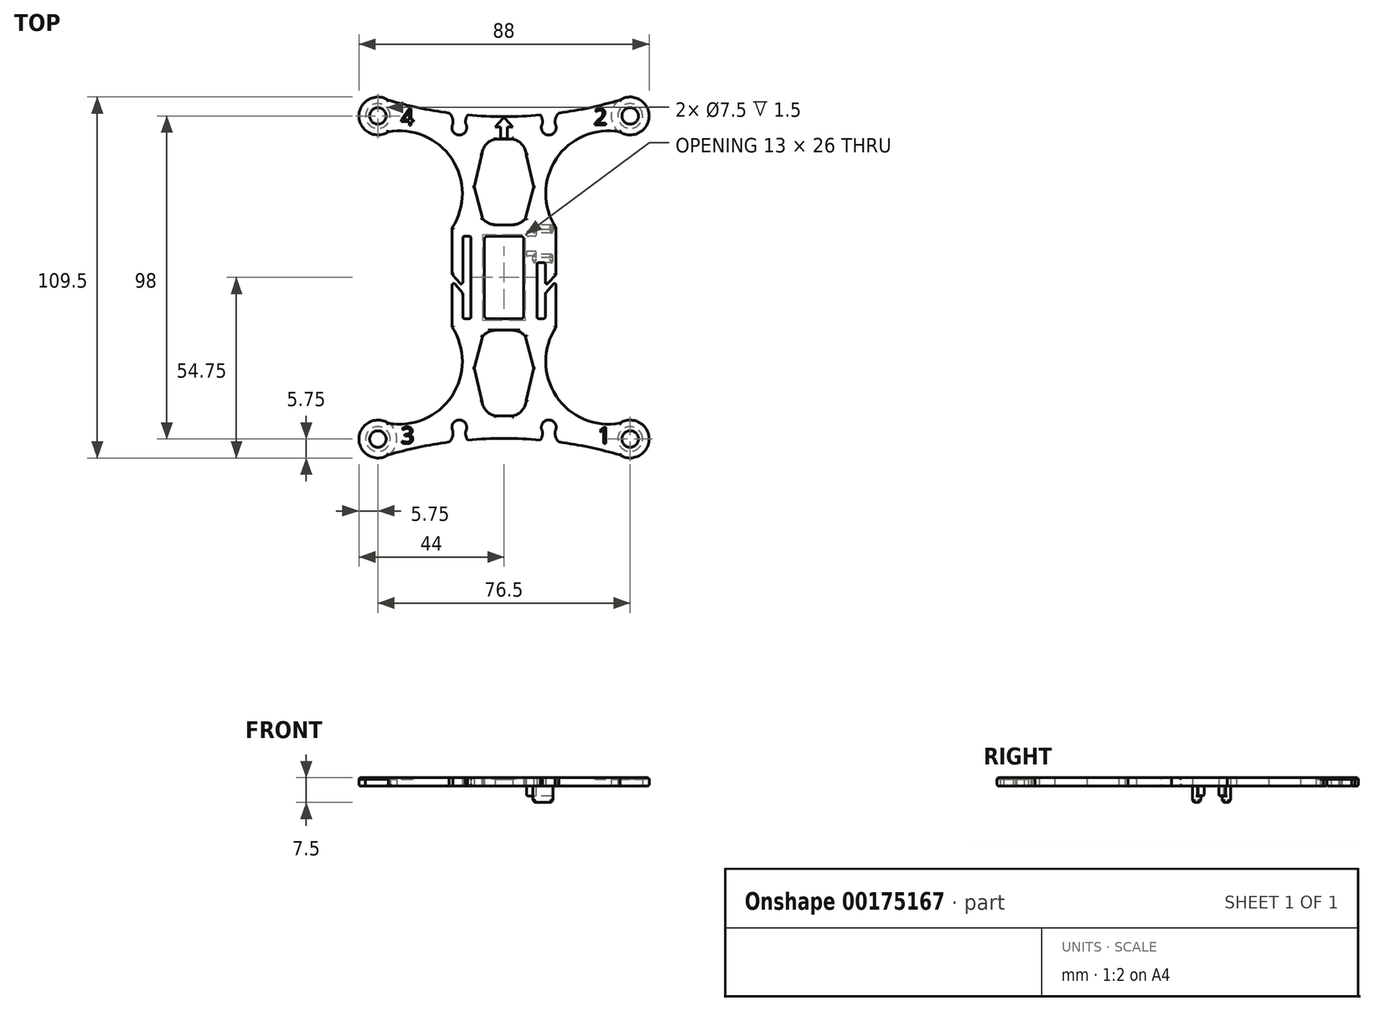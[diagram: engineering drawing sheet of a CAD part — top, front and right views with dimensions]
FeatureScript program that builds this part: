
annotation { "Feature Type Name" : "Feature", "Feature Type Description" : "" }
export const myFeature = defineFeature(function(context is Context, id is Id, definition is map)
    precondition{}
    {
        {
            var Q0;
            Q0=qCreatedBy(makeId("Top.planeOp"),FACE);
            var sketch = newSketch(context, id + "F0", { "sketchPlane" : qUnion([Q0])});
            skPoint(sketch, "E0.middle", {"position": v(0, 0) * mm});
            skCircle(sketch, "E1", {"center": v(-38.25, 49) * mm, "radius": 5.75 * mm});
            skCircle(sketch, "E2.MirrorC", {"center": v(38.25, 49) * mm, "radius": 5.75 * mm});
            skCircle(sketch, "E3.MirrorC", {"center": v(-38.25, -49) * mm, "radius": 5.75 * mm});
            skCircle(sketch, "E4.MirrorC", {"center": v(38.25, -49) * mm, "radius": 5.75 * mm});
            skArc(sketch, "E5", {"start": v(-35.12, 53.82) * mm, "mid": v(-25.97, 51.52) * mm, "end": v(-16.67, 49.9) * mm});
            skCircle(sketch, "E6", {"center": v(-38.25, 49) * mm, "radius": 3.75 * mm});
            skCircle(sketch, "E7.MirrorC", {"center": v(38.25, 49) * mm, "radius": 3.75 * mm});
            skCircle(sketch, "E8.MirrorC", {"center": v(38.25, -49) * mm, "radius": 3.75 * mm});
            skCircle(sketch, "E9.MirrorC", {"center": v(-38.25, -49) * mm, "radius": 3.75 * mm});
            skPoint(sketch, "E10.MirrorP", {"position": v(-9, -27.55) * mm});
            skArc(sketch, "E11.MirrorCS", {"start": v(-2.66, -42) * mm, "mid": v(-5.49, -40.33) * mm, "end": v(-6.7, -37.29) * mm});
            skArc(sketch, "E12.MirrorCS", {"start": v(-2.66, -16) * mm, "mid": v(-4.79, -16.51) * mm, "end": v(-6.5, -17.87) * mm});
            skLineSegment(sketch, "E13", {"start": v(-6.5, -17.87) * mm, "end": v(-9, -27.55) * mm});
            skLineSegment(sketch, "E14", {"start": v(-6.7, -37.29) * mm, "end": v(-9, -27.55) * mm});
            skArc(sketch, "E15.MirrorCS", {"start": v(2.66, -16) * mm, "mid": v(4.79, -16.51) * mm, "end": v(6.5, -17.87) * mm});
            skLineSegment(sketch, "E16.MirrorCS", {"start": v(6.5, -17.87) * mm, "end": v(9, -27.55) * mm});
            skLineSegment(sketch, "E17.MirrorCS", {"start": v(6.7, -37.29) * mm, "end": v(9, -27.55) * mm});
            skArc(sketch, "E18.MirrorCS", {"start": v(2.66, -42) * mm, "mid": v(5.49, -40.33) * mm, "end": v(6.7, -37.29) * mm});
            skLineSegment(sketch, "E19", {"start": v(-2.66, -16) * mm, "end": v(2.66, -16) * mm});
            skLineSegment(sketch, "E20", {"start": v(2.66, -42) * mm, "end": v(-2.66, -42) * mm});
            skLineSegment(sketch, "E21.MirrorCS", {"start": v(-2.66, 16) * mm, "end": v(2.66, 16) * mm});
            skArc(sketch, "E22.MirrorCS", {"start": v(-2.66, 16) * mm, "mid": v(-4.79, 16.51) * mm, "end": v(-6.5, 17.87) * mm});
            skLineSegment(sketch, "E23.MirrorCS", {"start": v(-6.5, 17.87) * mm, "end": v(-9, 27.55) * mm});
            skArc(sketch, "E24.MirrorCS", {"start": v(2.66, 16) * mm, "mid": v(4.79, 16.51) * mm, "end": v(6.5, 17.87) * mm});
            skLineSegment(sketch, "E25.MirrorCS", {"start": v(6.5, 17.87) * mm, "end": v(9, 27.55) * mm});
            skLineSegment(sketch, "E26.MirrorCS", {"start": v(-6.7, 37.29) * mm, "end": v(-9, 27.55) * mm});
            skLineSegment(sketch, "E27.MirrorCS", {"start": v(6.7, 37.29) * mm, "end": v(9, 27.55) * mm});
            skArc(sketch, "E28.MirrorCS", {"start": v(2.66, 42) * mm, "mid": v(5.49, 40.33) * mm, "end": v(6.7, 37.29) * mm});
            skLineSegment(sketch, "E29.MirrorCS", {"start": v(2.66, 42) * mm, "end": v(-2.66, 42) * mm});
            skArc(sketch, "E30.MirrorCS", {"start": v(-2.66, 42) * mm, "mid": v(-5.49, 40.33) * mm, "end": v(-6.7, 37.29) * mm});
            skArc(sketch, "E31", {"start": v(-15.79, 15) * mm, "mid": v(-15.82, 36) * mm, "end": v(-35.17, 44.14) * mm});
            skArc(sketch, "E32.MirrorCS", {"start": v(-35.12, -53.82) * mm, "mid": v(-25.97, -51.52) * mm, "end": v(-16.67, -49.9) * mm});
            skArc(sketch, "E33.MirrorCS", {"start": v(15.79, 15) * mm, "mid": v(15.82, 36) * mm, "end": v(35.17, 44.14) * mm});
            skArc(sketch, "E34.MirrorCS", {"start": v(15.79, -15) * mm, "mid": v(15.82, -36) * mm, "end": v(35.17, -44.14) * mm});
            skArc(sketch, "E35.MirrorCS", {"start": v(-15.79, -15) * mm, "mid": v(-15.82, -36) * mm, "end": v(-35.17, -44.14) * mm});
            skLineSegment(sketch, "E36", {"start": v(-15.79, 15) * mm, "end": v(15.79, 15) * mm, "construction": true});
            skLineSegment(sketch, "E37.MirrorCS", {"start": v(12, -12.5) * mm, "end": v(10.5, -12.5) * mm});
            skArc(sketch, "E38.MirrorCS", {"start": v(12.5, -12) * mm, "mid": v(12.35, -12.35) * mm, "end": v(12, -12.5) * mm});
            skArc(sketch, "E39.MirrorCS", {"start": v(10.5, -12.5) * mm, "mid": v(10.15, -12.35) * mm, "end": v(10, -12) * mm});
            skArc(sketch, "E40.trimOffspring", {"start": v(-11.03, 49.28) * mm, "mid": v(0, 48.79) * mm, "end": v(11.03, 49.28) * mm});
            skArc(sketch, "E41.MirrorCS", {"start": v(-11.6, 46.53) * mm, "mid": v(-11.6, 47.96) * mm, "end": v(-11.03, 49.28) * mm});
            skLineSegment(sketch, "E42.bottom", {"start": v(-5, 12.5) * mm, "end": v(5, 12.5) * mm});
            skLineSegment(sketch, "E42.top", {"start": v(-5, -12.5) * mm, "end": v(5, -12.5) * mm});
            skLineSegment(sketch, "E42.left", {"start": v(-6, 11.5) * mm, "end": v(-6, -11.5) * mm});
            skLineSegment(sketch, "E42.right", {"start": v(6, 11.5) * mm, "end": v(6, -11.5) * mm});
            skPoint(sketch, "E43.visualSharp", {"position": v(-6, 12.5) * mm});
            skArc(sketch, "E43.filletArc", {"start": v(-5, 12.5) * mm, "mid": v(-5.7, 12.2) * mm, "end": v(-6, 11.5) * mm});
            skArc(sketch, "E44.filletArc", {"start": v(6, 11.5) * mm, "mid": v(5.7, 12.2) * mm, "end": v(5, 12.5) * mm});
            skPoint(sketch, "E45.visualSharp", {"position": v(6, -12.5) * mm});
            skArc(sketch, "E45.filletArc", {"start": v(5, -12.5) * mm, "mid": v(5.7, -12.2) * mm, "end": v(6, -11.5) * mm});
            skPoint(sketch, "E46.visualSharp", {"position": v(-6, -12.5) * mm});
            skArc(sketch, "E46.filletArc", {"start": v(-6, -11.5) * mm, "mid": v(-5.7, -12.2) * mm, "end": v(-5, -12.5) * mm});
            skLineSegment(sketch, "E47", {"start": v(-15.79, -15) * mm, "end": v(-15.79, -2.33) * mm});
            skLineSegment(sketch, "E48", {"start": v(-15.79, 15) * mm, "end": v(-15.79, 1) * mm});
            skLineSegment(sketch, "E49.MirrorCS", {"start": v(-10, -12) * mm, "end": v(-10, 12) * mm});
            skLineSegment(sketch, "E50.MirrorCS", {"start": v(-12.5, -12) * mm, "end": v(-12.5, -4.77) * mm});
            skLineSegment(sketch, "E51.MirrorCS", {"start": v(-12, 12.5) * mm, "end": v(-10.5, 12.5) * mm});
            skArc(sketch, "E52.MirrorCS", {"start": v(-10, 12) * mm, "mid": v(-10.15, 12.35) * mm, "end": v(-10.5, 12.5) * mm});
            skArc(sketch, "E53.MirrorCS", {"start": v(-12, 12.5) * mm, "mid": v(-12.35, 12.35) * mm, "end": v(-12.5, 12) * mm});
            skArc(sketch, "E54.MirrorCS", {"start": v(-10.5, -12.5) * mm, "mid": v(-10.15, -12.35) * mm, "end": v(-10, -12) * mm});
            skLineSegment(sketch, "E55.MirrorCS", {"start": v(-12, -12.5) * mm, "end": v(-10.5, -12.5) * mm});
            skArc(sketch, "E56.MirrorCS", {"start": v(-12.5, -12) * mm, "mid": v(-12.35, -12.35) * mm, "end": v(-12, -12.5) * mm});
            skLineSegment(sketch, "E57", {"start": v(-14.91, -2) * mm, "end": v(-12.5, -4.77) * mm});
            skLineSegment(sketch, "E58", {"start": v(-15.79, 1) * mm, "end": v(-13.38, -1.76) * mm});
            skLineSegment(sketch, "E59.trimOffspring", {"start": v(-12.5, -1.43) * mm, "end": v(-12.5, 12) * mm});
            skPoint(sketch, "E60.visualSharp", {"position": v(-15.79, -1) * mm});
            skArc(sketch, "E60.filletArc", {"start": v(-14.91, -2) * mm, "mid": v(-15.47, -1.86) * mm, "end": v(-15.79, -2.33) * mm});
            skArc(sketch, "E61.filletArc", {"start": v(-13.38, -1.76) * mm, "mid": v(-12.82, -1.9) * mm, "end": v(-12.5, -1.43) * mm});
            skLineSegment(sketch, "E62.MirrorCS", {"start": v(12.5, -12) * mm, "end": v(12.5, -4.77) * mm});
            skLineSegment(sketch, "E63.MirrorCS", {"start": v(10, -12) * mm, "end": v(10, 4) * mm});
            skLineSegment(sketch, "E64.MirrorCS", {"start": v(14.91, -2) * mm, "end": v(12.5, -4.77) * mm});
            skLineSegment(sketch, "E65.MirrorCS", {"start": v(15.79, -15) * mm, "end": v(15.79, -2.33) * mm});
            skArc(sketch, "E66.MirrorCS", {"start": v(14.91, -2) * mm, "mid": v(15.47, -1.86) * mm, "end": v(15.79, -2.33) * mm});
            skArc(sketch, "E67.MirrorCS", {"start": v(13.38, -1.76) * mm, "mid": v(12.82, -1.9) * mm, "end": v(12.5, -1.43) * mm});
            skLineSegment(sketch, "E68.MirrorCS", {"start": v(12.5, -1.43) * mm, "end": v(12.5, 4) * mm});
            skLineSegment(sketch, "E69.MirrorCS", {"start": v(15.79, 1) * mm, "end": v(13.38, -1.76) * mm});
            skLineSegment(sketch, "E70.MirrorCS", {"start": v(15.79, 15) * mm, "end": v(15.79, 1) * mm});
            skPoint(sketch, "E71", {"position": v(10, 4.5) * mm});
            skPoint(sketch, "E72", {"position": v(12.5, 4.5) * mm});
            skLineSegment(sketch, "E73", {"start": v(10.5, 4.5) * mm, "end": v(12, 4.5) * mm});
            skArc(sketch, "E74.filletArc", {"start": v(10.5, 4.5) * mm, "mid": v(10.15, 4.35) * mm, "end": v(10, 4) * mm});
            skArc(sketch, "E75.filletArc", {"start": v(12.5, 4) * mm, "mid": v(12.35, 4.35) * mm, "end": v(12, 4.5) * mm});
            skPoint(sketch, "E76.visualSharp", {"position": v(8.79, 4.5) * mm});
            skPoint(sketch, "E77.visualSharp", {"position": v(14.79, 4.5) * mm});
            skArc(sketch, "E78.trimOffspring", {"start": v(16.67, 49.9) * mm, "mid": v(25.97, 51.52) * mm, "end": v(35.12, 53.82) * mm});
            skArc(sketch, "E79.trimOffspring", {"start": v(16.67, -49.9) * mm, "mid": v(25.97, -51.52) * mm, "end": v(35.12, -53.82) * mm});
            skArc(sketch, "E80.trimOffspring", {"start": v(-11.03, -49.28) * mm, "mid": v(0, -48.79) * mm, "end": v(11.03, -49.28) * mm});
            skLineSegment(sketch, "E81", {"start": v(17.22, 49.98) * mm, "end": v(17.22, 49.98) * mm});
            skLineSegment(sketch, "E82.MirrorCS", {"start": v(17.22, -49.98) * mm, "end": v(17.22, -49.98) * mm});
            skArc(sketch, "E83.MirrorCS", {"start": v(-15.54, 46.53) * mm, "mid": v(-15.65, 48.37) * mm, "end": v(-16.67, 49.9) * mm});
            skArc(sketch, "E84.trimOffspring", {"start": v(-15.54, 46.53) * mm, "mid": v(-13.57, 43.2) * mm, "end": v(-11.6, 46.53) * mm});
            skArc(sketch, "E85.MirrorCS", {"start": v(11.6, 46.53) * mm, "mid": v(11.6, 47.96) * mm, "end": v(11.03, 49.28) * mm});
            skArc(sketch, "E86.MirrorCS", {"start": v(15.54, 46.53) * mm, "mid": v(13.57, 43.2) * mm, "end": v(11.6, 46.53) * mm});
            skArc(sketch, "E87.MirrorCS", {"start": v(15.54, 46.53) * mm, "mid": v(15.65, 48.37) * mm, "end": v(16.67, 49.9) * mm});
            skArc(sketch, "E88.MirrorCS", {"start": v(15.54, -46.53) * mm, "mid": v(13.57, -43.2) * mm, "end": v(11.6, -46.53) * mm});
            skArc(sketch, "E89.MirrorCS", {"start": v(15.54, -46.53) * mm, "mid": v(15.65, -48.37) * mm, "end": v(16.67, -49.9) * mm});
            skArc(sketch, "E90.MirrorCS", {"start": v(11.6, -46.53) * mm, "mid": v(11.6, -47.96) * mm, "end": v(11.03, -49.28) * mm});
            skArc(sketch, "E91.MirrorCS", {"start": v(-15.54, -46.53) * mm, "mid": v(-15.65, -48.37) * mm, "end": v(-16.67, -49.9) * mm});
            skArc(sketch, "E92.MirrorCS", {"start": v(-11.6, -46.53) * mm, "mid": v(-11.6, -47.96) * mm, "end": v(-11.03, -49.28) * mm});
            skArc(sketch, "E93.MirrorCS", {"start": v(-15.54, -46.53) * mm, "mid": v(-13.57, -43.2) * mm, "end": v(-11.6, -46.53) * mm});
            skSolve(sketch);
        }
        {
            var Q0;
            {var subQ4=sQuery(id+"F0.wireOp",EDGE,"E5");Q0=makeQuery(id+"F0.imprint","IMPRINT",FACE,{"disambiguationData":[TD([[makeQuery(id+"F0.imprint","IMPRINT",EDGE,{"derivedFrom":subQ4}),-1.0]])]});}
            var Q1;
            {var subQ0=sQuery(id+"F0.wireOp",EDGE,"7a08c846-7200-404a-ab22-a396ae0e95b40.MirrorCS");Q1=makeQuery(id+"F0.imprint","IMPRINT",FACE,{"disambiguationData":[TD([[makeQuery(id+"F0.imprint","IMPRINT",EDGE,{"derivedFrom":subQ0}),-1.0]])]});}
            var Q2;
            {var subQ0=sQuery(id+"F0.wireOp",EDGE,"SV39OC4L-nHPT-JrW3-9Lr1-tMvvluVvlcrm");Q2=makeQuery(id+"F0.imprint","IMPRINT",FACE,{"disambiguationData":[TD([[makeQuery(id+"F0.imprint","IMPRINT",EDGE,{"derivedFrom":subQ0}),1.0]])]});}
            var Q3;
            {var subQ2=sQuery(id+"F0.wireOp",EDGE,"KmvPTI4Y-Ru9T-GGZq-2kg1-KeB8K268cKMw.top");Q3=makeQuery(id+"F0.imprint","IMPRINT",FACE,{"disambiguationData":[TD([[makeQuery(id+"F0.imprint","IMPRINT",EDGE,{"derivedFrom":subQ2}),-1.0]])]});}
            var Q4;
            Q4=makeQuery(id+"F0.imprint","IMPRINT",FACE,{"disambiguationData":[TD([[makeQuery(id+"F0.imprint","IMPRINT",EDGE,{"derivedFrom":sQuery(id+"F0.wireOp",EDGE,"TM0b15PC-G09Y-eCJG-wMI8-OMJ6jJeQZKML.top")}),1.0]])]});
            var Q5;
            Q5=makeQuery(id+"F0.imprint","IMPRINT",FACE,{"disambiguationData":[TD([[makeQuery(id+"F0.imprint","IMPRINT",EDGE,{"derivedFrom":sQuery(id+"F0.wireOp",EDGE,"3d6d2522-cb81-429b-89e0-43078ca379200.MirrorCS")}),-1.0]])]});
            var Q6;
            {var subQ1=sQuery(id+"F0.wireOp",EDGE,"f26be708-061c-449e-934f-b77e1b1d895a0.MirrorCS");Q6=makeQuery(id+"F0.imprint","IMPRINT",FACE,{"disambiguationData":[TD([[makeQuery(id+"F0.imprint","IMPRINT",EDGE,{"derivedFrom":subQ1}),-1.0]])]});}
            extrude(context, id + "F1", {"entities" : qUnion([Q0, Q1, Q2, Q3, Q4, Q5, Q6]), "depth" : 2.5 * mm});
        }
        {
            var Q0;
            Q0=makeQuery(id+"F0.imprint","IMPRINT",FACE,{"disambiguationData":[TD([[makeQuery(id+"F0.imprint","IMPRINT",EDGE,{"derivedFrom":sQuery(id+"F0.wireOp",EDGE,"E6")}),-1.0]])]});
            var Q1;
            Q1=makeQuery(id+"F0.imprint","IMPRINT",FACE,{"disambiguationData":[TD([[makeQuery(id+"F0.imprint","IMPRINT",EDGE,{"derivedFrom":sQuery(id+"F0.wireOp",EDGE,"E7.MirrorC")}),1.0]])]});
            var Q2;
            Q2=makeQuery(id+"F0.imprint","IMPRINT",FACE,{"disambiguationData":[TD([[makeQuery(id+"F0.imprint","IMPRINT",EDGE,{"derivedFrom":sQuery(id+"F0.wireOp",EDGE,"E8.MirrorC")}),-1.0]])]});
            var Q3;
            Q3=makeQuery(id+"F0.imprint","IMPRINT",FACE,{"disambiguationData":[TD([[makeQuery(id+"F0.imprint","IMPRINT",EDGE,{"derivedFrom":sQuery(id+"F0.wireOp",EDGE,"E9.MirrorC")}),1.0]])]});
            extrude(context, id + "F2", {"entities" : qUnion([Q0, Q1, Q2, Q3]), "operationType" : NewBodyOperationType.ADD, "depth" : 2 * mm});
        }
        {
            var Q0;
            Q0=makeQuery(id+"F1.opExtrude","CAP_FACE",FACE,{"disambiguationData":[OSD([sQuery(id+"F0.wireOp",EDGE,"E1"),sQuery(id+"F0.wireOp",EDGE,"E2.MirrorC"),sQuery(id+"F0.wireOp",EDGE,"E3.MirrorC"),sQuery(id+"F0.wireOp",EDGE,"E4.MirrorC"),sQuery(id+"F0.wireOp",EDGE,"E5"),sQuery(id+"F0.wireOp",EDGE,"E6"),sQuery(id+"F0.wireOp",EDGE,"E7.MirrorC"),sQuery(id+"F0.wireOp",EDGE,"E8.MirrorC"),sQuery(id+"F0.wireOp",EDGE,"E9.MirrorC"),sQuery(id+"F0.wireOp",EDGE,"vB4YpJxw-nM1r-KAMU-Z2z7-AA1Xbjjr12VQ"),sQuery(id+"F0.wireOp",EDGE,"e54bd452-817c-44b1-b4a1-4a82a5b737490.MirrorC"),sQuery(id+"F0.wireOp",EDGE,"5ae8c34d-aa19-45d0-b816-4b0481c35e6e0.MirrorC"),sQuery(id+"F0.wireOp",EDGE,"3a3e3443-e76c-4b3f-931a-bba0a9ca54bb0.MirrorC"),sQuery(id+"F0.wireOp",EDGE,"E11.MirrorCS"),sQuery(id+"F0.wireOp",EDGE,"E12.MirrorCS"),sQuery(id+"F0.wireOp",EDGE,"E13"),sQuery(id+"F0.wireOp",EDGE,"E14"),sQuery(id+"F0.wireOp",EDGE,"E15.MirrorCS"),sQuery(id+"F0.wireOp",EDGE,"E16.MirrorCS"),sQuery(id+"F0.wireOp",EDGE,"E17.MirrorCS"),sQuery(id+"F0.wireOp",EDGE,"E18.MirrorCS"),sQuery(id+"F0.wireOp",EDGE,"E19"),sQuery(id+"F0.wireOp",EDGE,"E20"),sQuery(id+"F0.wireOp",EDGE,"E21.MirrorCS"),sQuery(id+"F0.wireOp",EDGE,"E22.MirrorCS"),sQuery(id+"F0.wireOp",EDGE,"E23.MirrorCS"),sQuery(id+"F0.wireOp",EDGE,"E24.MirrorCS"),sQuery(id+"F0.wireOp",EDGE,"E25.MirrorCS"),sQuery(id+"F0.wireOp",EDGE,"E26.MirrorCS"),sQuery(id+"F0.wireOp",EDGE,"E27.MirrorCS"),sQuery(id+"F0.wireOp",EDGE,"E28.MirrorCS"),sQuery(id+"F0.wireOp",EDGE,"E29.MirrorCS"),sQuery(id+"F0.wireOp",EDGE,"E30.MirrorCS"),sQuery(id+"F0.wireOp",EDGE,"E31"),sQuery(id+"F0.wireOp",EDGE,"E32.MirrorCS"),sQuery(id+"F0.wireOp",EDGE,"E33.MirrorCS"),sQuery(id+"F0.wireOp",EDGE,"E34.MirrorCS"),sQuery(id+"F0.wireOp",EDGE,"E35.MirrorCS"),sQuery(id+"F0.wireOp",EDGE,"fVDweLas-wsoK-wS6S-1z9Y-dXXYinH5IBTg"),sQuery(id+"F0.wireOp",EDGE,"DgQ3zJUJ-pF02-0TgB-KWvi-qXfrHXNG7Bep.bottom"),sQuery(id+"F0.wireOp",EDGE,"DgQ3zJUJ-pF02-0TgB-KWvi-qXfrHXNG7Bep.top"),sQuery(id+"F0.wireOp",EDGE,"DgQ3zJUJ-pF02-0TgB-KWvi-qXfrHXNG7Bep.left"),sQuery(id+"F0.wireOp",EDGE,"DgQ3zJUJ-pF02-0TgB-KWvi-qXfrHXNG7Bep.right"),sQuery(id+"F0.wireOp",EDGE,"c76fb391-d7de-4dc3-a68f-2a06cb2f6573.filletArc"),sQuery(id+"F0.wireOp",EDGE,"5654feee-e0ec-4d14-bcde-d39bc1d4a277.filletArc"),sQuery(id+"F0.wireOp",EDGE,"a181469e-c1a0-4d89-87a1-cba4924c182a.filletArc"),sQuery(id+"F0.wireOp",EDGE,"6285ec27-b856-43d4-bfe6-c4aa6bb2cc4e.filletArc"),sQuery(id+"F0.wireOp",EDGE,"E37.MirrorCS"),sQuery(id+"F0.wireOp",EDGE,"E38.MirrorCS"),sQuery(id+"F0.wireOp",EDGE,"E39.MirrorCS"),sQuery(id+"F0.wireOp",EDGE,"6c157492-324c-4fe9-82e5-da5673b074dd0.MirrorCS"),sQuery(id+"F0.wireOp",EDGE,"5ab077b0-c7e9-45b7-be53-f71d1ae10c3f0.MirrorCS"),sQuery(id+"F0.wireOp",EDGE,"fc55cce6-b858-4ce9-87a1-b3bd53c235ab0.MirrorCS"),sQuery(id+"F0.wireOp",EDGE,"9f491082-fd4d-4411-bae9-10bea509d7400.MirrorCS"),sQuery(id+"F0.wireOp",EDGE,"1b0662fc-7704-42c9-b5fa-9ce22a18d3f90.MirrorCS"),sQuery(id+"F0.wireOp",EDGE,"QFYX3ccx-0vfA-8Ihh-7p7o-tATHIodxN48p"),sQuery(id+"F0.wireOp",EDGE,"E40.trimOffspring"),sQuery(id+"F0.wireOp",EDGE,"qH3YTvKd-Peeo-Apzx-g0Uu-npIK0QSimt1m"),sQuery(id+"F0.wireOp",EDGE,"HBzP5cjg-J4kx-zMse-p9Wa-D2NjmpWyf6zF"),sQuery(id+"F0.wireOp",EDGE,"b30a117b-d75a-4502-b387-7b125c7515d1.trimOffspring"),sQuery(id+"F0.wireOp",EDGE,"Q6oGcjuH-qqtT-cDzR-LXAg-flI4N5uVv7ns"),sQuery(id+"F0.wireOp",EDGE,"E41.MirrorCS"),sQuery(id+"F0.wireOp",EDGE,"NQUfp69C-25it-PKYB-2tBc-24tSypLDHoPc"),sQuery(id+"F0.wireOp",EDGE,"c989e6c5-f976-4a01-a2df-d995f657efa90.MirrorCS"),sQuery(id+"F0.wireOp",EDGE,"15c0fab1-d19e-4163-b076-96272f6b97990.MirrorCS"),sQuery(id+"F0.wireOp",EDGE,"37e26e7e-321b-4c47-af7c-8b72d8fa4a340.MirrorCS"),sQuery(id+"F0.wireOp",EDGE,"0fc43aed-00d9-4609-b4de-8f51d0ed3c1b0.MirrorCS"),sQuery(id+"F0.wireOp",EDGE,"ec73fb21-01e8-4369-aab7-f5da74862bec0.MirrorCS"),sQuery(id+"F0.wireOp",EDGE,"92f736b5-5a78-439e-ae92-a389169262630.MirrorCS"),sQuery(id+"F0.wireOp",EDGE,"d2bba0ee-929f-40cb-a0b9-0c6ccd42c60c0.MirrorCS"),sQuery(id+"F0.wireOp",EDGE,"95becd90-c284-490f-9980-00c66b97ee920.MirrorCS"),sQuery(id+"F0.wireOp",EDGE,"17a50fb4-b6d3-4921-a8fa-819a7e347bdf0.MirrorCS"),sQuery(id+"F0.wireOp",EDGE,"0a836e34-2154-49af-98e0-05fdf2c9219c0.MirrorCS"),sQuery(id+"F0.wireOp",EDGE,"69461dee-d267-421c-9efa-fca9b703b25c0.MirrorCS"),sQuery(id+"F0.wireOp",EDGE,"E42.bottom"),sQuery(id+"F0.wireOp",EDGE,"E42.top"),sQuery(id+"F0.wireOp",EDGE,"E42.left"),sQuery(id+"F0.wireOp",EDGE,"E42.right"),sQuery(id+"F0.wireOp",EDGE,"E43.filletArc"),sQuery(id+"F0.wireOp",EDGE,"E44.filletArc"),sQuery(id+"F0.wireOp",EDGE,"E45.filletArc"),sQuery(id+"F0.wireOp",EDGE,"E46.filletArc")])],"isStart":false});
            var sketch = newSketch(context, id + "F3", { "sketchPlane" : qUnion([Q0])});
            skLineSegment(sketch, "E94", {"start": v(-1, 42.11) * mm, "end": v(-1, 45.61) * mm});
            skLineSegment(sketch, "E95", {"start": v(-1, 45.61) * mm, "end": v(-2.66, 45.61) * mm});
            skLineSegment(sketch, "E96", {"start": v(-2.66, 45.61) * mm, "end": v(0, 48.6) * mm});
            skLineSegment(sketch, "E97.MirrorCS", {"start": v(2.66, 45.61) * mm, "end": v(0, 48.6) * mm});
            skLineSegment(sketch, "E98.MirrorCS", {"start": v(1, 45.61) * mm, "end": v(2.66, 45.61) * mm});
            skLineSegment(sketch, "E99.MirrorCS", {"start": v(1, 42.11) * mm, "end": v(1, 45.61) * mm});
            skLineSegment(sketch, "E100", {"start": v(-1, 42.11) * mm, "end": v(1, 42.11) * mm});
            skText(sketch, "E101", { "text": "1", "fontName": "OpenSans-Regular.ttf"});
            skText(sketch, "E102", { "text": "3", "fontName": "OpenSans-Regular.ttf"});
            skText(sketch, "E103", { "text": "2", "fontName": "OpenSans-Regular.ttf"});
            skText(sketch, "E104", { "text": "4", "fontName": "OpenSans-Regular.ttf"});
            const initialGuessF3  = {"E101": [0.02838, -0.05039, 1, 0, 0.005], "E102": [-0.03125, -0.05033, 1, 0, 0.005], "E103": [0.0272, 0.04623, 1, 0, 0.005], "E104": [-0.03125, 0.0462, 1, 0, 0.005]};
            skSetInitialGuess(sketch, initialGuessF3);
            skSolve(sketch);
        }
        {
            var Q0;
            Q0 = qSketchRegion(id + "F3", true);
            extrude(context, id + "F4", {"entities" : qUnion([Q0]), "operationType" : NewBodyOperationType.REMOVE, "oppositeDirection" : true, "depth" : .5 * mm});
        }
        {
            var Q0;
            Q0=makeQuery(id+"F1.opExtrude","CAP_FACE",FACE,{"disambiguationData":[OSD([sQuery(id+"F0.wireOp",EDGE,"E1"),sQuery(id+"F0.wireOp",EDGE,"E2.MirrorC"),sQuery(id+"F0.wireOp",EDGE,"E3.MirrorC"),sQuery(id+"F0.wireOp",EDGE,"E4.MirrorC"),sQuery(id+"F0.wireOp",EDGE,"E5"),sQuery(id+"F0.wireOp",EDGE,"E6"),sQuery(id+"F0.wireOp",EDGE,"E7.MirrorC"),sQuery(id+"F0.wireOp",EDGE,"E8.MirrorC"),sQuery(id+"F0.wireOp",EDGE,"E9.MirrorC"),sQuery(id+"F0.wireOp",EDGE,"vB4YpJxw-nM1r-KAMU-Z2z7-AA1Xbjjr12VQ"),sQuery(id+"F0.wireOp",EDGE,"e54bd452-817c-44b1-b4a1-4a82a5b737490.MirrorC"),sQuery(id+"F0.wireOp",EDGE,"5ae8c34d-aa19-45d0-b816-4b0481c35e6e0.MirrorC"),sQuery(id+"F0.wireOp",EDGE,"3a3e3443-e76c-4b3f-931a-bba0a9ca54bb0.MirrorC"),sQuery(id+"F0.wireOp",EDGE,"E11.MirrorCS"),sQuery(id+"F0.wireOp",EDGE,"E12.MirrorCS"),sQuery(id+"F0.wireOp",EDGE,"E13"),sQuery(id+"F0.wireOp",EDGE,"E14"),sQuery(id+"F0.wireOp",EDGE,"E15.MirrorCS"),sQuery(id+"F0.wireOp",EDGE,"E16.MirrorCS"),sQuery(id+"F0.wireOp",EDGE,"E17.MirrorCS"),sQuery(id+"F0.wireOp",EDGE,"E18.MirrorCS"),sQuery(id+"F0.wireOp",EDGE,"E19"),sQuery(id+"F0.wireOp",EDGE,"E20"),sQuery(id+"F0.wireOp",EDGE,"E21.MirrorCS"),sQuery(id+"F0.wireOp",EDGE,"E22.MirrorCS"),sQuery(id+"F0.wireOp",EDGE,"E23.MirrorCS"),sQuery(id+"F0.wireOp",EDGE,"E24.MirrorCS"),sQuery(id+"F0.wireOp",EDGE,"E25.MirrorCS"),sQuery(id+"F0.wireOp",EDGE,"E26.MirrorCS"),sQuery(id+"F0.wireOp",EDGE,"E27.MirrorCS"),sQuery(id+"F0.wireOp",EDGE,"E28.MirrorCS"),sQuery(id+"F0.wireOp",EDGE,"E29.MirrorCS"),sQuery(id+"F0.wireOp",EDGE,"E30.MirrorCS"),sQuery(id+"F0.wireOp",EDGE,"E31"),sQuery(id+"F0.wireOp",EDGE,"E32.MirrorCS"),sQuery(id+"F0.wireOp",EDGE,"E33.MirrorCS"),sQuery(id+"F0.wireOp",EDGE,"E34.MirrorCS"),sQuery(id+"F0.wireOp",EDGE,"E35.MirrorCS"),sQuery(id+"F0.wireOp",EDGE,"E37.MirrorCS"),sQuery(id+"F0.wireOp",EDGE,"E38.MirrorCS"),sQuery(id+"F0.wireOp",EDGE,"E39.MirrorCS"),sQuery(id+"F0.wireOp",EDGE,"E40.trimOffspring"),sQuery(id+"F0.wireOp",EDGE,"qH3YTvKd-Peeo-Apzx-g0Uu-npIK0QSimt1m"),sQuery(id+"F0.wireOp",EDGE,"HBzP5cjg-J4kx-zMse-p9Wa-D2NjmpWyf6zF"),sQuery(id+"F0.wireOp",EDGE,"b30a117b-d75a-4502-b387-7b125c7515d1.trimOffspring"),sQuery(id+"F0.wireOp",EDGE,"Q6oGcjuH-qqtT-cDzR-LXAg-flI4N5uVv7ns"),sQuery(id+"F0.wireOp",EDGE,"E41.MirrorCS"),sQuery(id+"F0.wireOp",EDGE,"NQUfp69C-25it-PKYB-2tBc-24tSypLDHoPc"),sQuery(id+"F0.wireOp",EDGE,"c989e6c5-f976-4a01-a2df-d995f657efa90.MirrorCS"),sQuery(id+"F0.wireOp",EDGE,"15c0fab1-d19e-4163-b076-96272f6b97990.MirrorCS"),sQuery(id+"F0.wireOp",EDGE,"37e26e7e-321b-4c47-af7c-8b72d8fa4a340.MirrorCS"),sQuery(id+"F0.wireOp",EDGE,"0fc43aed-00d9-4609-b4de-8f51d0ed3c1b0.MirrorCS"),sQuery(id+"F0.wireOp",EDGE,"ec73fb21-01e8-4369-aab7-f5da74862bec0.MirrorCS"),sQuery(id+"F0.wireOp",EDGE,"92f736b5-5a78-439e-ae92-a389169262630.MirrorCS"),sQuery(id+"F0.wireOp",EDGE,"d2bba0ee-929f-40cb-a0b9-0c6ccd42c60c0.MirrorCS"),sQuery(id+"F0.wireOp",EDGE,"95becd90-c284-490f-9980-00c66b97ee920.MirrorCS"),sQuery(id+"F0.wireOp",EDGE,"17a50fb4-b6d3-4921-a8fa-819a7e347bdf0.MirrorCS"),sQuery(id+"F0.wireOp",EDGE,"0a836e34-2154-49af-98e0-05fdf2c9219c0.MirrorCS"),sQuery(id+"F0.wireOp",EDGE,"69461dee-d267-421c-9efa-fca9b703b25c0.MirrorCS"),sQuery(id+"F0.wireOp",EDGE,"E42.bottom"),sQuery(id+"F0.wireOp",EDGE,"E42.top"),sQuery(id+"F0.wireOp",EDGE,"E42.left"),sQuery(id+"F0.wireOp",EDGE,"E42.right"),sQuery(id+"F0.wireOp",EDGE,"E43.filletArc"),sQuery(id+"F0.wireOp",EDGE,"E44.filletArc"),sQuery(id+"F0.wireOp",EDGE,"E45.filletArc"),sQuery(id+"F0.wireOp",EDGE,"E46.filletArc"),sQuery(id+"F0.wireOp",EDGE,"E47"),sQuery(id+"F0.wireOp",EDGE,"E48"),sQuery(id+"F0.wireOp",EDGE,"E49.MirrorCS"),sQuery(id+"F0.wireOp",EDGE,"E50.MirrorCS"),sQuery(id+"F0.wireOp",EDGE,"E51.MirrorCS"),sQuery(id+"F0.wireOp",EDGE,"E52.MirrorCS"),sQuery(id+"F0.wireOp",EDGE,"E53.MirrorCS"),sQuery(id+"F0.wireOp",EDGE,"E54.MirrorCS"),sQuery(id+"F0.wireOp",EDGE,"E55.MirrorCS"),sQuery(id+"F0.wireOp",EDGE,"E56.MirrorCS"),sQuery(id+"F0.wireOp",EDGE,"E57"),sQuery(id+"F0.wireOp",EDGE,"E58"),sQuery(id+"F0.wireOp",EDGE,"E59.trimOffspring"),sQuery(id+"F0.wireOp",EDGE,"E60.filletArc"),sQuery(id+"F0.wireOp",EDGE,"E61.filletArc"),sQuery(id+"F0.wireOp",EDGE,"E62.MirrorCS"),sQuery(id+"F0.wireOp",EDGE,"E63.MirrorCS"),sQuery(id+"F0.wireOp",EDGE,"E64.MirrorCS"),sQuery(id+"F0.wireOp",EDGE,"E65.MirrorCS"),sQuery(id+"F0.wireOp",EDGE,"E66.MirrorCS"),sQuery(id+"F0.wireOp",EDGE,"E67.MirrorCS"),sQuery(id+"F0.wireOp",EDGE,"E68.MirrorCS"),sQuery(id+"F0.wireOp",EDGE,"E69.MirrorCS"),sQuery(id+"F0.wireOp",EDGE,"E70.MirrorCS"),sQuery(id+"F0.wireOp",EDGE,"E73"),sQuery(id+"F0.wireOp",EDGE,"E74.filletArc"),sQuery(id+"F0.wireOp",EDGE,"E75.filletArc")])],"isStart":true});
            var sketch = newSketch(context, id + "F5", { "sketchPlane" : qUnion([Q0])});
            skLineSegment(sketch, "E105.bottom", {"start": v(14.29, -4.5) * mm, "end": v(9.29, -4.5) * mm});
            skLineSegment(sketch, "E105.top", {"start": v(14.29, -6) * mm, "end": v(9.79, -6) * mm});
            skLineSegment(sketch, "E105.left", {"start": v(14.79, -5) * mm, "end": v(14.79, -5.5) * mm});
            skLineSegment(sketch, "E105.right", {"start": v(8.79, -5) * mm, "end": v(8.79, -6) * mm});
            skLineSegment(sketch, "E106.left", {"start": v(9.79, -6) * mm, "end": v(9.79, -6.5) * mm});
            skLineSegment(sketch, "E106.right", {"start": v(8.79, -6) * mm, "end": v(8.79, -6.5) * mm});
            skLineSegment(sketch, "E107.bottom", {"start": v(8.79, -6.5) * mm, "end": v(7.29, -6.5) * mm});
            skLineSegment(sketch, "E107.top", {"start": v(9.29, -8) * mm, "end": v(7.29, -8) * mm});
            skLineSegment(sketch, "E107.left", {"start": v(9.79, -6.5) * mm, "end": v(9.79, -7.5) * mm});
            skLineSegment(sketch, "E107.right", {"start": v(6.79, -7) * mm, "end": v(6.79, -7.5) * mm});
            skPoint(sketch, "E108.visualSharp", {"position": v(6.79, -6.5) * mm});
            skArc(sketch, "E108.filletArc", {"start": v(7.29, -6.5) * mm, "mid": v(6.94, -6.65) * mm, "end": v(6.79, -7) * mm});
            skPoint(sketch, "E109.visualSharp", {"position": v(6.79, -8) * mm});
            skArc(sketch, "E109.filletArc", {"start": v(6.79, -7.5) * mm, "mid": v(6.94, -7.85) * mm, "end": v(7.29, -8) * mm});
            skPoint(sketch, "E110.visualSharp", {"position": v(9.79, -8) * mm});
            skArc(sketch, "E110.filletArc", {"start": v(9.29, -8) * mm, "mid": v(9.64, -7.85) * mm, "end": v(9.79, -7.5) * mm});
            skPoint(sketch, "E111.visualSharp", {"position": v(14.79, -6) * mm});
            skArc(sketch, "E111.filletArc", {"start": v(14.29, -6) * mm, "mid": v(14.64, -5.85) * mm, "end": v(14.79, -5.5) * mm});
            skPoint(sketch, "E112", {"position": v(14.79, -4.5) * mm});
            skArc(sketch, "E113.filletArc", {"start": v(14.79, -5) * mm, "mid": v(14.64, -4.65) * mm, "end": v(14.29, -4.5) * mm});
            skPoint(sketch, "E114", {"position": v(8.79, -4.5) * mm});
            skArc(sketch, "E115.filletArc", {"start": v(9.29, -4.5) * mm, "mid": v(8.94, -4.65) * mm, "end": v(8.79, -5) * mm});
            skLineSegment(sketch, "E116", {"start": v(6.79, -8) * mm, "end": v(6.79, -12.5) * mm, "construction": true});
            skPoint(sketch, "E117", {"position": v(6.79, -10.25) * mm});
            skLineSegment(sketch, "E118", {"start": v(6.79, -10.25) * mm, "end": v(15.79, -10.25) * mm, "construction": true});
            skLineSegment(sketch, "E119.MirrorCS", {"start": v(9.29, -12.5) * mm, "end": v(7.29, -12.5) * mm});
            skArc(sketch, "E120.MirrorCS", {"start": v(6.79, -13) * mm, "mid": v(6.94, -12.65) * mm, "end": v(7.29, -12.5) * mm});
            skLineSegment(sketch, "E121.MirrorCS", {"start": v(6.79, -13.5) * mm, "end": v(6.79, -13) * mm});
            skArc(sketch, "E122.MirrorCS", {"start": v(7.29, -14) * mm, "mid": v(6.94, -13.85) * mm, "end": v(6.79, -13.5) * mm});
            skLineSegment(sketch, "E123.MirrorCS", {"start": v(8.79, -14) * mm, "end": v(7.29, -14) * mm});
            skLineSegment(sketch, "E124.MirrorCS", {"start": v(9.79, -14) * mm, "end": v(9.79, -13) * mm});
            skArc(sketch, "E125.MirrorCS", {"start": v(9.29, -12.5) * mm, "mid": v(9.64, -12.65) * mm, "end": v(9.79, -13) * mm});
            skLineSegment(sketch, "E126.MirrorCS", {"start": v(8.79, -14.5) * mm, "end": v(8.79, -14) * mm});
            skLineSegment(sketch, "E127.MirrorCS", {"start": v(9.79, -14.5) * mm, "end": v(9.79, -14) * mm});
            skLineSegment(sketch, "E128.MirrorCS", {"start": v(8.79, -15.5) * mm, "end": v(8.79, -14.5) * mm});
            skArc(sketch, "E129.MirrorCS", {"start": v(9.29, -16) * mm, "mid": v(8.94, -15.85) * mm, "end": v(8.79, -15.5) * mm});
            skLineSegment(sketch, "E130.MirrorCS", {"start": v(14.29, -14.5) * mm, "end": v(9.79, -14.5) * mm});
            skLineSegment(sketch, "E131.MirrorCS", {"start": v(14.29, -16) * mm, "end": v(9.29, -16) * mm});
            skArc(sketch, "E132.MirrorCS", {"start": v(14.29, -14.5) * mm, "mid": v(14.64, -14.65) * mm, "end": v(14.79, -15) * mm});
            skLineSegment(sketch, "E133.MirrorCS", {"start": v(14.79, -15.5) * mm, "end": v(14.79, -15) * mm});
            skArc(sketch, "E134.MirrorCS", {"start": v(14.79, -15.5) * mm, "mid": v(14.64, -15.85) * mm, "end": v(14.29, -16) * mm});
            skPoint(sketch, "E135.orphan", {"position": v(8.79, -14.5) * mm});
            skSolve(sketch);
        }
        {
            var Q0;
            Q0 = qSketchRegion(id + "F5", true);
            extrude(context, id + "F6", {"entities" : qUnion([Q0]), "operationType" : NewBodyOperationType.ADD, "depth" : 3 * mm});
        }
        {
            var Q0;
            Q0=makeQuery(id+"F6.opExtrude","CAP_FACE",FACE,{"disambiguationData":[OSD([sQuery(id+"F5.wireOp",EDGE,"E105.bottom"),sQuery(id+"F5.wireOp",EDGE,"E105.top"),sQuery(id+"F5.wireOp",EDGE,"E105.left"),sQuery(id+"F5.wireOp",EDGE,"E105.right"),sQuery(id+"F5.wireOp",EDGE,"E106.left"),sQuery(id+"F5.wireOp",EDGE,"E106.right"),sQuery(id+"F5.wireOp",EDGE,"E107.bottom"),sQuery(id+"F5.wireOp",EDGE,"E107.top"),sQuery(id+"F5.wireOp",EDGE,"E107.left"),sQuery(id+"F5.wireOp",EDGE,"E107.right"),sQuery(id+"F5.wireOp",EDGE,"E108.filletArc"),sQuery(id+"F5.wireOp",EDGE,"E109.filletArc"),sQuery(id+"F5.wireOp",EDGE,"E110.filletArc"),sQuery(id+"F5.wireOp",EDGE,"E111.filletArc"),sQuery(id+"F5.wireOp",EDGE,"E113.filletArc"),sQuery(id+"F5.wireOp",EDGE,"E115.filletArc")])],"isStart":false});
            var sketch = newSketch(context, id + "F7", { "sketchPlane" : qUnion([Q0])});
            skPoint(sketch, "E136.firstSnap0", {"position": v(14.64, -4.65) * mm});
            skLineSegment(sketch, "E136.bottom", {"start": v(14.29, -4.5) * mm, "end": v(9.29, -4.5) * mm});
            skLineSegment(sketch, "E136.top", {"start": v(14.29, -7) * mm, "end": v(9.29, -7) * mm});
            skLineSegment(sketch, "E136.left", {"start": v(14.79, -5) * mm, "end": v(14.79, -6.5) * mm});
            skLineSegment(sketch, "E136.right", {"start": v(8.79, -5) * mm, "end": v(8.79, -6.5) * mm});
            skPoint(sketch, "E137.visualSharp", {"position": v(14.79, -4.5) * mm});
            skArc(sketch, "E137.filletArc", {"start": v(14.79, -5) * mm, "mid": v(14.64, -4.65) * mm, "end": v(14.29, -4.5) * mm});
            skPoint(sketch, "E138.visualSharp", {"position": v(8.79, -4.5) * mm});
            skArc(sketch, "E138.filletArc", {"start": v(9.29, -4.5) * mm, "mid": v(8.94, -4.65) * mm, "end": v(8.79, -5) * mm});
            skPoint(sketch, "E139.visualSharp", {"position": v(14.79, -7) * mm});
            skArc(sketch, "E139.filletArc", {"start": v(14.29, -7) * mm, "mid": v(14.64, -6.85) * mm, "end": v(14.79, -6.5) * mm});
            skLineSegment(sketch, "E140", {"start": v(8.79, -7) * mm, "end": v(8.79, -13.5) * mm, "construction": true});
            skPoint(sketch, "E141", {"position": v(8.79, -10.25) * mm});
            skLineSegment(sketch, "E142", {"start": v(8.79, -10.25) * mm, "end": v(15.78, -10.25) * mm, "construction": true});
            skLineSegment(sketch, "E143.MirrorCS", {"start": v(14.29, -13.5) * mm, "end": v(9.29, -13.5) * mm});
            skLineSegment(sketch, "E144.MirrorCS", {"start": v(8.79, -15.5) * mm, "end": v(8.79, -14) * mm});
            skLineSegment(sketch, "E145.MirrorCS", {"start": v(14.29, -16) * mm, "end": v(9.29, -16) * mm});
            skArc(sketch, "E146.MirrorCS", {"start": v(9.29, -16) * mm, "mid": v(8.94, -15.85) * mm, "end": v(8.79, -15.5) * mm});
            skArc(sketch, "E147.MirrorCS", {"start": v(14.79, -15.5) * mm, "mid": v(14.64, -15.85) * mm, "end": v(14.29, -16) * mm});
            skLineSegment(sketch, "E148.MirrorCS", {"start": v(14.79, -15.5) * mm, "end": v(14.79, -14) * mm});
            skArc(sketch, "E149.MirrorCS", {"start": v(14.29, -13.5) * mm, "mid": v(14.64, -13.65) * mm, "end": v(14.79, -14) * mm});
            skPoint(sketch, "E150.visualSharp", {"position": v(8.79, -7) * mm});
            skArc(sketch, "E150.filletArc", {"start": v(8.79, -6.5) * mm, "mid": v(8.94, -6.85) * mm, "end": v(9.29, -7) * mm});
            skPoint(sketch, "E151.visualSharp", {"position": v(8.79, -13.5) * mm});
            skArc(sketch, "E151.filletArc", {"start": v(9.29, -13.5) * mm, "mid": v(8.94, -13.65) * mm, "end": v(8.79, -14) * mm});
            skSolve(sketch);
        }
        {
            var Q0;
            Q0=makeQuery(id+"F7.imprint","IMPRINT",FACE,{"disambiguationData":[TD([[makeQuery(id+"F7.imprint","IMPRINT",EDGE,{"derivedFrom":sQuery(id+"F7.wireOp",EDGE,"E143.MirrorCS")}),1.0]])]});
            var Q1;
            Q1=makeQuery(id+"F7.imprint","IMPRINT",FACE,{"disambiguationData":[TD([[makeQuery(id+"F7.imprint","IMPRINT",EDGE,{"derivedFrom":sQuery(id+"F7.wireOp",EDGE,"E136.bottom")}),1.0]])]});
            var Q2;
            {var subQ0=sQuery(id+"F7.wireOp",EDGE,"E139.filletArc");Q2=makeQuery(id+"F7.imprint","IMPRINT",FACE,{"disambiguationData":[TD([[makeQuery(id+"F7.imprint","IMPRINT",EDGE,{"derivedFrom":subQ0}),1.0]])]});}
            extrude(context, id + "F8", {"entities" : qUnion([Q0, Q1, Q2]), "operationType" : NewBodyOperationType.ADD, "depth" : 2 * mm});
        }
        {
            var Q0;
            Q0=makeQuery(id+"F8.opExtrude","CAP_EDGE",EDGE,{"disambiguationData":[OSD([sQuery(id+"F7.wireOp",EDGE,"E145.MirrorCS")])],"isStart":false});
            var Q1;
            Q1=makeQuery(id+"F8.opExtrude","CAP_EDGE",EDGE,{"disambiguationData":[OSD([sQuery(id+"F7.wireOp",EDGE,"E143.MirrorCS")])],"isStart":false});
            var Q2;
            Q2=makeQuery(id+"F8.opExtrude","CAP_EDGE",EDGE,{"disambiguationData":[OSD([sQuery(id+"F7.wireOp",EDGE,"E151.filletArc")])],"isStart":false});
            var Q3;
            Q3=makeQuery(id+"F8.opExtrude","CAP_EDGE",EDGE,{"disambiguationData":[OSD([sQuery(id+"F7.wireOp",EDGE,"E144.MirrorCS")])],"isStart":false});
            var Q4;
            Q4=makeQuery(id+"F8.opExtrude","CAP_EDGE",EDGE,{"disambiguationData":[OSD([sQuery(id+"F7.wireOp",EDGE,"E146.MirrorCS")])],"isStart":false});
            var Q5;
            Q5=makeQuery(id+"F8.opExtrude","CAP_EDGE",EDGE,{"disambiguationData":[OSD([sQuery(id+"F7.wireOp",EDGE,"E147.MirrorCS")])],"isStart":false});
            var Q6;
            Q6=makeQuery(id+"F8.opExtrude","CAP_EDGE",EDGE,{"disambiguationData":[OSD([sQuery(id+"F7.wireOp",EDGE,"E148.MirrorCS")])],"isStart":false});
            var Q7;
            Q7=makeQuery(id+"F8.opExtrude","CAP_EDGE",EDGE,{"disambiguationData":[OSD([sQuery(id+"F7.wireOp",EDGE,"E149.MirrorCS")])],"isStart":false});
            var Q8;
            Q8=makeQuery(id+"F8.opExtrude","CAP_EDGE",EDGE,{"disambiguationData":[OSD([sQuery(id+"F7.wireOp",EDGE,"E136.top")])],"isStart":false});
            var Q9;
            Q9=makeQuery(id+"F8.opExtrude","CAP_EDGE",EDGE,{"disambiguationData":[OSD([sQuery(id+"F7.wireOp",EDGE,"E139.filletArc")])],"isStart":false});
            var Q10;
            Q10=makeQuery(id+"F8.opExtrude","CAP_EDGE",EDGE,{"disambiguationData":[OSD([sQuery(id+"F7.wireOp",EDGE,"E136.left")])],"isStart":false});
            var Q11;
            Q11=makeQuery(id+"F8.opExtrude","CAP_EDGE",EDGE,{"disambiguationData":[OSD([sQuery(id+"F7.wireOp",EDGE,"E136.bottom")])],"isStart":false});
            var Q12;
            Q12=makeQuery(id+"F8.opExtrude","CAP_EDGE",EDGE,{"disambiguationData":[OSD([sQuery(id+"F7.wireOp",EDGE,"E137.filletArc")])],"isStart":false});
            var Q13;
            Q13=makeQuery(id+"F8.opExtrude","CAP_EDGE",EDGE,{"disambiguationData":[OSD([sQuery(id+"F7.wireOp",EDGE,"E138.filletArc")])],"isStart":false});
            var Q14;
            Q14=makeQuery(id+"F8.opExtrude","CAP_EDGE",EDGE,{"disambiguationData":[OSD([sQuery(id+"F7.wireOp",EDGE,"E136.right")])],"isStart":false});
            var Q15;
            Q15=makeQuery(id+"F8.opExtrude","CAP_EDGE",EDGE,{"disambiguationData":[OSD([sQuery(id+"F7.wireOp",EDGE,"E150.filletArc")])],"isStart":false});
            fillet(context, id + "F9", {"entities" : qUnion([Q0, Q1, Q2, Q3, Q4, Q5, Q6, Q7, Q8, Q9, Q10, Q11, Q12, Q13, Q14, Q15]), "radius" : 1 * mm, "tangentPropagation" : true, "allowEdgeOverflow" : false});
        }
        {
            var Q0;
            Q0=makeQuery(id+"F6.opExtrude","CAP_EDGE",EDGE,{"disambiguationData":[OSD([sQuery(id+"F5.wireOp",EDGE,"E122.MirrorCS")])],"isStart":false});
            var Q1;
            Q1=makeQuery(id+"F6.opExtrude","CAP_EDGE",EDGE,{"disambiguationData":[OSD([sQuery(id+"F5.wireOp",EDGE,"E109.filletArc")])],"isStart":false});
            fillet(context, id + "F10", {"entities" : qUnion([Q0, Q1]), "radius" : .5 * mm, "tangentPropagation" : true, "allowEdgeOverflow" : false});
        }
        {
            var Q0;
            Q0=makeQuery(id+"F1.opExtrude","CAP_EDGE",EDGE,{"disambiguationData":[OSD([sQuery(id+"F0.wireOp",EDGE,"E42.left")])],"isStart":false});
            var Q1;
            Q1=makeQuery(id+"F1.opExtrude","CAP_EDGE",EDGE,{"disambiguationData":[OSD([sQuery(id+"F0.wireOp",EDGE,"E20")])],"isStart":false});
            var Q2;
            Q2=makeQuery(id+"F1.opExtrude","CAP_EDGE",EDGE,{"disambiguationData":[OSD([sQuery(id+"F0.wireOp",EDGE,"E12.MirrorCS")])],"isStart":false});
            var Q3;
            Q3=makeQuery(id+"F1.opExtrude","CAP_EDGE",EDGE,{"disambiguationData":[OSD([sQuery(id+"F0.wireOp",EDGE,"E13")])],"isStart":false});
            var Q4;
            Q4=makeQuery(id+"F1.opExtrude","CAP_EDGE",EDGE,{"disambiguationData":[OSD([sQuery(id+"F0.wireOp",EDGE,"E14")])],"isStart":false});
            var Q5;
            Q5=makeQuery(id+"F1.opExtrude","CAP_EDGE",EDGE,{"disambiguationData":[OSD([sQuery(id+"F0.wireOp",EDGE,"E11.MirrorCS")])],"isStart":false});
            var Q6;
            Q6=makeQuery(id+"F1.opExtrude","CAP_EDGE",EDGE,{"disambiguationData":[OSD([sQuery(id+"F0.wireOp",EDGE,"E15.MirrorCS")])],"isStart":false});
            var Q7;
            Q7=makeQuery(id+"F1.opExtrude","CAP_EDGE",EDGE,{"disambiguationData":[OSD([sQuery(id+"F0.wireOp",EDGE,"E16.MirrorCS")])],"isStart":false});
            var Q8;
            Q8=makeQuery(id+"F1.opExtrude","CAP_EDGE",EDGE,{"disambiguationData":[OSD([sQuery(id+"F0.wireOp",EDGE,"E17.MirrorCS")])],"isStart":false});
            var Q9;
            Q9=makeQuery(id+"F1.opExtrude","CAP_EDGE",EDGE,{"disambiguationData":[OSD([sQuery(id+"F0.wireOp",EDGE,"E18.MirrorCS")])],"isStart":false});
            var Q10;
            Q10=makeQuery(id+"F1.opExtrude","CAP_EDGE",EDGE,{"disambiguationData":[OSD([sQuery(id+"F0.wireOp",EDGE,"E30.MirrorCS")])],"isStart":false});
            var Q11;
            Q11=makeQuery(id+"F1.opExtrude","CAP_EDGE",EDGE,{"disambiguationData":[OSD([sQuery(id+"F0.wireOp",EDGE,"E29.MirrorCS")])],"isStart":false});
            var Q12;
            Q12=makeQuery(id+"F1.opExtrude","CAP_EDGE",EDGE,{"disambiguationData":[OSD([sQuery(id+"F0.wireOp",EDGE,"E28.MirrorCS")])],"isStart":false});
            var Q13;
            Q13=makeQuery(id+"F1.opExtrude","CAP_EDGE",EDGE,{"disambiguationData":[OSD([sQuery(id+"F0.wireOp",EDGE,"E27.MirrorCS")])],"isStart":false});
            var Q14;
            Q14=makeQuery(id+"F1.opExtrude","CAP_EDGE",EDGE,{"disambiguationData":[OSD([sQuery(id+"F0.wireOp",EDGE,"E25.MirrorCS")])],"isStart":false});
            var Q15;
            Q15=makeQuery(id+"F1.opExtrude","CAP_EDGE",EDGE,{"disambiguationData":[OSD([sQuery(id+"F0.wireOp",EDGE,"E21.MirrorCS")])],"isStart":false});
            var Q16;
            Q16=makeQuery(id+"F1.opExtrude","CAP_EDGE",EDGE,{"disambiguationData":[OSD([sQuery(id+"F0.wireOp",EDGE,"E24.MirrorCS")])],"isStart":false});
            var Q17;
            Q17=makeQuery(id+"F1.opExtrude","CAP_EDGE",EDGE,{"disambiguationData":[OSD([sQuery(id+"F0.wireOp",EDGE,"E23.MirrorCS")])],"isStart":false});
            var Q18;
            Q18=makeQuery(id+"F1.opExtrude","CAP_EDGE",EDGE,{"disambiguationData":[OSD([sQuery(id+"F0.wireOp",EDGE,"E22.MirrorCS")])],"isStart":false});
            var Q19;
            Q19=makeQuery(id+"F1.opExtrude","CAP_EDGE",EDGE,{"disambiguationData":[OSD([sQuery(id+"F0.wireOp",EDGE,"E26.MirrorCS")])],"isStart":false});
            var Q20;
            Q20=makeQuery(id+"F1.opExtrude","CAP_EDGE",EDGE,{"disambiguationData":[OSD([sQuery(id+"F0.wireOp",EDGE,"E42.right")])],"isStart":true});
            var Q21;
            Q21=makeQuery(id+"F1.opExtrude","CAP_EDGE",EDGE,{"disambiguationData":[OSD([sQuery(id+"F0.wireOp",EDGE,"E25.MirrorCS")])],"isStart":true});
            var Q22;
            Q22=makeQuery(id+"F1.opExtrude","CAP_EDGE",EDGE,{"disambiguationData":[OSD([sQuery(id+"F0.wireOp",EDGE,"E24.MirrorCS")])],"isStart":true});
            var Q23;
            Q23=makeQuery(id+"F1.opExtrude","CAP_EDGE",EDGE,{"disambiguationData":[OSD([sQuery(id+"F0.wireOp",EDGE,"E21.MirrorCS")])],"isStart":true});
            var Q24;
            Q24=makeQuery(id+"F1.opExtrude","CAP_EDGE",EDGE,{"disambiguationData":[OSD([sQuery(id+"F0.wireOp",EDGE,"E23.MirrorCS")])],"isStart":true});
            var Q25;
            Q25=makeQuery(id+"F1.opExtrude","CAP_EDGE",EDGE,{"disambiguationData":[OSD([sQuery(id+"F0.wireOp",EDGE,"E26.MirrorCS")])],"isStart":true});
            var Q26;
            Q26=makeQuery(id+"F1.opExtrude","CAP_EDGE",EDGE,{"disambiguationData":[OSD([sQuery(id+"F0.wireOp",EDGE,"E30.MirrorCS")])],"isStart":true});
            var Q27;
            Q27=makeQuery(id+"F1.opExtrude","CAP_EDGE",EDGE,{"disambiguationData":[OSD([sQuery(id+"F0.wireOp",EDGE,"E29.MirrorCS")])],"isStart":true});
            var Q28;
            Q28=makeQuery(id+"F1.opExtrude","CAP_EDGE",EDGE,{"disambiguationData":[OSD([sQuery(id+"F0.wireOp",EDGE,"E28.MirrorCS")])],"isStart":true});
            var Q29;
            Q29=makeQuery(id+"F1.opExtrude","CAP_EDGE",EDGE,{"disambiguationData":[OSD([sQuery(id+"F0.wireOp",EDGE,"E27.MirrorCS")])],"isStart":true});
            var Q30;
            Q30=makeQuery(id+"F1.opExtrude","CAP_EDGE",EDGE,{"disambiguationData":[OSD([sQuery(id+"F0.wireOp",EDGE,"E17.MirrorCS")])],"isStart":true});
            var Q31;
            Q31=makeQuery(id+"F1.opExtrude","CAP_EDGE",EDGE,{"disambiguationData":[OSD([sQuery(id+"F0.wireOp",EDGE,"E18.MirrorCS")])],"isStart":true});
            var Q32;
            Q32=makeQuery(id+"F1.opExtrude","CAP_EDGE",EDGE,{"disambiguationData":[OSD([sQuery(id+"F0.wireOp",EDGE,"E20")])],"isStart":true});
            var Q33;
            Q33=makeQuery(id+"F1.opExtrude","CAP_EDGE",EDGE,{"disambiguationData":[OSD([sQuery(id+"F0.wireOp",EDGE,"E11.MirrorCS")])],"isStart":true});
            var Q34;
            Q34=makeQuery(id+"F1.opExtrude","CAP_EDGE",EDGE,{"disambiguationData":[OSD([sQuery(id+"F0.wireOp",EDGE,"E14")])],"isStart":true});
            var Q35;
            Q35=makeQuery(id+"F1.opExtrude","CAP_EDGE",EDGE,{"disambiguationData":[OSD([sQuery(id+"F0.wireOp",EDGE,"E13")])],"isStart":true});
            var Q36;
            Q36=makeQuery(id+"F1.opExtrude","CAP_EDGE",EDGE,{"disambiguationData":[OSD([sQuery(id+"F0.wireOp",EDGE,"E16.MirrorCS")])],"isStart":true});
            var Q37;
            Q37=makeQuery(id+"F1.opExtrude","CAP_EDGE",EDGE,{"disambiguationData":[OSD([sQuery(id+"F0.wireOp",EDGE,"E15.MirrorCS")])],"isStart":true});
            var Q38;
            Q38=makeQuery(id+"F1.opExtrude","CAP_EDGE",EDGE,{"disambiguationData":[OSD([sQuery(id+"F0.wireOp",EDGE,"E19")])],"isStart":true});
            var Q39;
            Q39=makeQuery(id+"F1.opExtrude","CAP_EDGE",EDGE,{"disambiguationData":[OSD([sQuery(id+"F0.wireOp",EDGE,"E12.MirrorCS")])],"isStart":true});
            fillet(context, id + "F11", {"entities" : qUnion([Q0, Q1, Q2, Q3, Q4, Q5, Q6, Q7, Q8, Q9, Q10, Q11, Q12, Q13, Q14, Q15, Q16, Q17, Q18, Q19, Q20, Q21, Q22, Q23, Q24, Q25, Q26, Q27, Q28, Q29, Q30, Q31, Q32, Q33, Q34, Q35, Q36, Q37, Q38, Q39]), "radius" : .5 * mm, "tangentPropagation" : true, "allowEdgeOverflow" : false});
        }
        {
            var Q0;
            Q0=makeQuery(id+"F1.opExtrude","CAP_EDGE",EDGE,{"disambiguationData":[OSD([sQuery(id+"F0.wireOp",EDGE,"E49.MirrorCS")])],"isStart":true});
            var Q1;
            Q1=makeQuery(id+"F1.opExtrude","CAP_EDGE",EDGE,{"disambiguationData":[OSD([sQuery(id+"F0.wireOp",EDGE,"E63.MirrorCS")])],"isStart":true});
            var Q2;
            Q2=makeQuery(id+"F1.opExtrude","CAP_EDGE",EDGE,{"disambiguationData":[OSD([sQuery(id+"F0.wireOp",EDGE,"E49.MirrorCS")])],"isStart":false});
            var Q3;
            Q3=makeQuery(id+"F1.opExtrude","CAP_EDGE",EDGE,{"disambiguationData":[OSD([sQuery(id+"F0.wireOp",EDGE,"E63.MirrorCS")])],"isStart":false});
            fillet(context, id + "F12", {"entities" : qUnion([Q0, Q1, Q2, Q3]), "radius" : .5 * mm, "tangentPropagation" : true, "allowEdgeOverflow" : false});
        }
        {
            var Q0;
            Q0=makeQuery(id+"F1.opExtrude","CAP_EDGE",EDGE,{"disambiguationData":[OSD([sQuery(id+"F0.wireOp",EDGE,"E48")])],"isStart":false});
            var Q1;
            Q1=makeQuery(id+"F1.opExtrude","CAP_EDGE",EDGE,{"disambiguationData":[OSD([sQuery(id+"F0.wireOp",EDGE,"E31")])],"isStart":false});
            var Q2;
            Q2=makeQuery(id+"F1.opExtrude","CAP_EDGE",EDGE,{"disambiguationData":[OSD([sQuery(id+"F0.wireOp",EDGE,"E33.MirrorCS")])],"isStart":false});
            var Q3;
            Q3=makeQuery(id+"F1.opExtrude","CAP_EDGE",EDGE,{"disambiguationData":[OSD([sQuery(id+"F0.wireOp",EDGE,"E70.MirrorCS")])],"isStart":false});
            var Q4;
            Q4=makeQuery(id+"F1.opExtrude","CAP_EDGE",EDGE,{"disambiguationData":[OSD([sQuery(id+"F0.wireOp",EDGE,"E65.MirrorCS")])],"isStart":false});
            var Q5;
            Q5=makeQuery(id+"F1.opExtrude","CAP_EDGE",EDGE,{"disambiguationData":[OSD([sQuery(id+"F0.wireOp",EDGE,"E47")])],"isStart":false});
            var Q6;
            Q6=makeQuery(id+"F1.opExtrude","CAP_EDGE",EDGE,{"disambiguationData":[OSD([sQuery(id+"F0.wireOp",EDGE,"29c33aa2-e30d-4d77-a239-c7a4e06ad0fa.trimOffspring")])],"isStart":false});
            var Q7;
            Q7=makeQuery(id+"F1.opExtrude","CAP_EDGE",EDGE,{"disambiguationData":[OSD([sQuery(id+"F0.wireOp",EDGE,"E79.trimOffspring")])],"isStart":false});
            var Q8;
            Q8=makeQuery(id+"F1.opExtrude","CAP_EDGE",EDGE,{"disambiguationData":[OSD([sQuery(id+"F0.wireOp",EDGE,"E34.MirrorCS")])],"isStart":false});
            var Q9;
            Q9=makeQuery(id+"F1.opExtrude","CAP_EDGE",EDGE,{"disambiguationData":[OSD([sQuery(id+"F0.wireOp",EDGE,"E78.trimOffspring")])],"isStart":false});
            var Q10;
            Q10=makeQuery(id+"F1.opExtrude","CAP_EDGE",EDGE,{"disambiguationData":[OSD([sQuery(id+"F0.wireOp",EDGE,"E40.trimOffspring")])],"isStart":false});
            var Q11;
            Q11=makeQuery(id+"F1.opExtrude","CAP_EDGE",EDGE,{"disambiguationData":[OSD([sQuery(id+"F0.wireOp",EDGE,"E5")])],"isStart":false});
            var Q12;
            Q12=makeQuery(id+"F1.opExtrude","CAP_EDGE",EDGE,{"disambiguationData":[OSD([sQuery(id+"F0.wireOp",EDGE,"E33.MirrorCS")])],"isStart":true});
            var Q13;
            Q13=makeQuery(id+"F1.opExtrude","CAP_EDGE",EDGE,{"disambiguationData":[OSD([sQuery(id+"F0.wireOp",EDGE,"E2.MirrorC")])],"isStart":true});
            var Q14;
            Q14=makeQuery(id+"F1.opExtrude","CAP_EDGE",EDGE,{"disambiguationData":[OSD([sQuery(id+"F0.wireOp",EDGE,"E78.trimOffspring")])],"isStart":true});
            var Q15;
            Q15=makeQuery(id+"F1.opExtrude","CAP_EDGE",EDGE,{"disambiguationData":[OSD([sQuery(id+"F0.wireOp",EDGE,"E40.trimOffspring")])],"isStart":true});
            var Q16;
            Q16=makeQuery(id+"F1.opExtrude","CAP_EDGE",EDGE,{"disambiguationData":[OSD([sQuery(id+"F0.wireOp",EDGE,"E5")])],"isStart":true});
            var Q17;
            Q17=makeQuery(id+"F1.opExtrude","CAP_EDGE",EDGE,{"disambiguationData":[OSD([sQuery(id+"F0.wireOp",EDGE,"E1")])],"isStart":true});
            var Q18;
            Q18=makeQuery(id+"F1.opExtrude","CAP_EDGE",EDGE,{"disambiguationData":[OSD([sQuery(id+"F0.wireOp",EDGE,"E31")])],"isStart":true});
            var Q19;
            Q19=makeQuery(id+"F1.opExtrude","CAP_EDGE",EDGE,{"disambiguationData":[OSD([sQuery(id+"F0.wireOp",EDGE,"E48")])],"isStart":true});
            var Q20;
            Q20=makeQuery(id+"F1.opExtrude","CAP_EDGE",EDGE,{"disambiguationData":[OSD([sQuery(id+"F0.wireOp",EDGE,"E47")])],"isStart":true});
            var Q21;
            Q21=makeQuery(id+"F1.opExtrude","CAP_EDGE",EDGE,{"disambiguationData":[OSD([sQuery(id+"F0.wireOp",EDGE,"E70.MirrorCS")])],"isStart":true});
            var Q22;
            Q22=makeQuery(id+"F1.opExtrude","CAP_EDGE",EDGE,{"disambiguationData":[OSD([sQuery(id+"F0.wireOp",EDGE,"E65.MirrorCS")])],"isStart":true});
            var Q23;
            Q23=makeQuery(id+"F1.opExtrude","CAP_EDGE",EDGE,{"disambiguationData":[OSD([sQuery(id+"F0.wireOp",EDGE,"E34.MirrorCS")])],"isStart":true});
            var Q24;
            Q24=makeQuery(id+"F1.opExtrude","CAP_EDGE",EDGE,{"disambiguationData":[OSD([sQuery(id+"F0.wireOp",EDGE,"E35.MirrorCS")])],"isStart":true});
            var Q25;
            Q25=makeQuery(id+"F1.opExtrude","CAP_EDGE",EDGE,{"disambiguationData":[OSD([sQuery(id+"F0.wireOp",EDGE,"E4.MirrorC")])],"isStart":true});
            var Q26;
            Q26=makeQuery(id+"F1.opExtrude","CAP_EDGE",EDGE,{"disambiguationData":[OSD([sQuery(id+"F0.wireOp",EDGE,"E3.MirrorC")])],"isStart":true});
            var Q27;
            Q27=makeQuery(id+"F1.opExtrude","CAP_EDGE",EDGE,{"disambiguationData":[OSD([sQuery(id+"F0.wireOp",EDGE,"29c33aa2-e30d-4d77-a239-c7a4e06ad0fa.trimOffspring")])],"isStart":true});
            var Q28;
            Q28=makeQuery(id+"F1.opExtrude","CAP_EDGE",EDGE,{"disambiguationData":[OSD([sQuery(id+"F0.wireOp",EDGE,"E32.MirrorCS")])],"isStart":true});
            var Q29;
            Q29=makeQuery(id+"F1.opExtrude","CAP_EDGE",EDGE,{"disambiguationData":[OSD([sQuery(id+"F0.wireOp",EDGE,"E79.trimOffspring")])],"isStart":true});
            var Q30;
            Q30=makeQuery(id+"F1.opExtrude","CAP_EDGE",EDGE,{"disambiguationData":[OSD([sQuery(id+"F0.wireOp",EDGE,"E32.MirrorCS")])],"isStart":false});
            var Q31;
            Q31=makeQuery(id+"F1.opExtrude","CAP_EDGE",EDGE,{"disambiguationData":[OSD([sQuery(id+"F0.wireOp",EDGE,"E35.MirrorCS")])],"isStart":false});
            fillet(context, id + "F13", {"entities" : qUnion([Q0, Q1, Q2, Q3, Q4, Q5, Q6, Q7, Q8, Q9, Q10, Q11, Q12, Q13, Q14, Q15, Q16, Q17, Q18, Q19, Q20, Q21, Q22, Q23, Q24, Q25, Q26, Q27, Q28, Q29, Q30, Q31]), "radius" : .5 * mm, "tangentPropagation" : true, "allowEdgeOverflow" : false});
        }
        {
            var Q0;
            Q0=makeQuery(id+"F2.opExtrude","CAP_FACE",FACE,{"disambiguationData":[OSD([sQuery(id+"F0.wireOp",EDGE,"E3.MirrorC"),sQuery(id+"F0.wireOp",EDGE,"E9.MirrorC")])],"isStart":false});
            var sketch = newSketch(context, id + "F14", { "sketchPlane" : qUnion([Q0])});
            skCircle(sketch, "E152", {"center": v(-38.25, -49) * mm, "radius": 5.75 * mm});
            skCircle(sketch, "E153", {"center": v(-38.25, -49) * mm, "radius": 2.5 * mm});
            skCircle(sketch, "E154.MirrorC", {"center": v(38.25, -49) * mm, "radius": 5.75 * mm});
            skCircle(sketch, "E155.MirrorC", {"center": v(38.25, -49) * mm, "radius": 2.5 * mm});
            skCircle(sketch, "E156.MirrorC", {"center": v(-38.25, 49) * mm, "radius": 5.75 * mm});
            skCircle(sketch, "E157.MirrorC", {"center": v(-38.25, 49) * mm, "radius": 2.5 * mm});
            skCircle(sketch, "E158.MirrorC", {"center": v(38.25, 49) * mm, "radius": 5.75 * mm});
            skCircle(sketch, "E159.MirrorC", {"center": v(38.25, 49) * mm, "radius": 2.5 * mm});
            skSolve(sketch);
        }
        {
            var Q0;
            Q0 = qSketchRegion(id + "F14", true);
            extrude(context, id + "F15", {"entities" : qUnion([Q0]), "operationType" : NewBodyOperationType.ADD, "depth" : .5 * mm});
        }
        {
            var Q0;
            Q0=makeQuery(id+"F2.opExtrude","CAP_EDGE",EDGE,{"disambiguationData":[OSD([sQuery(id+"F0.wireOp",EDGE,"E9.MirrorC")])],"isStart":true});
            var Q1;
            Q1=makeQuery(id+"F15.opExtrude","CAP_EDGE",EDGE,{"disambiguationData":[OSD([sQuery(id+"F14.wireOp",EDGE,"E153")])],"isStart":false});
            var Q2;
            Q2=makeQuery(id+"F15.opExtrude","CAP_EDGE",EDGE,{"disambiguationData":[OSD([sQuery(id+"F14.wireOp",EDGE,"E152")])],"isStart":false});
            var Q3;
            Q3=makeQuery(id+"F2.opExtrude","CAP_EDGE",EDGE,{"disambiguationData":[OSD([sQuery(id+"F0.wireOp",EDGE,"E3.MirrorC")])],"isStart":true});
            var Q4;
            Q4=makeQuery(id+"F15.opExtrude","CAP_EDGE",EDGE,{"disambiguationData":[OSD([sQuery(id+"F14.wireOp",EDGE,"E154.MirrorC")])],"isStart":false});
            var Q5;
            Q5=makeQuery(id+"F15.opExtrude","CAP_EDGE",EDGE,{"disambiguationData":[OSD([sQuery(id+"F14.wireOp",EDGE,"E155.MirrorC")])],"isStart":false});
            var Q6;
            Q6=makeQuery(id+"F2.opExtrude","CAP_EDGE",EDGE,{"disambiguationData":[OSD([sQuery(id+"F0.wireOp",EDGE,"E4.MirrorC")])],"isStart":true});
            var Q7;
            Q7=makeQuery(id+"F2.opExtrude","CAP_EDGE",EDGE,{"disambiguationData":[OSD([sQuery(id+"F0.wireOp",EDGE,"E7.MirrorC")])],"isStart":true});
            var Q8;
            Q8=makeQuery(id+"F15.opExtrude","CAP_EDGE",EDGE,{"disambiguationData":[OSD([sQuery(id+"F14.wireOp",EDGE,"E159.MirrorC")])],"isStart":false});
            var Q9;
            Q9=makeQuery(id+"F15.opExtrude","CAP_EDGE",EDGE,{"disambiguationData":[OSD([sQuery(id+"F14.wireOp",EDGE,"E158.MirrorC")])],"isStart":false});
            var Q10;
            Q10=makeQuery(id+"F2.opExtrude","CAP_EDGE",EDGE,{"disambiguationData":[OSD([sQuery(id+"F0.wireOp",EDGE,"E2.MirrorC")])],"isStart":true});
            var Q11;
            Q11=makeQuery(id+"F2.opExtrude","CAP_EDGE",EDGE,{"disambiguationData":[OSD([sQuery(id+"F0.wireOp",EDGE,"E1")])],"isStart":true});
            var Q12;
            Q12=makeQuery(id+"F2.opExtrude","CAP_EDGE",EDGE,{"disambiguationData":[OSD([sQuery(id+"F0.wireOp",EDGE,"E6")])],"isStart":true});
            var Q13;
            Q13=makeQuery(id+"F15.opExtrude","CAP_EDGE",EDGE,{"disambiguationData":[OSD([sQuery(id+"F14.wireOp",EDGE,"E156.MirrorC")])],"isStart":false});
            var Q14;
            Q14=makeQuery(id+"F15.opExtrude","CAP_EDGE",EDGE,{"disambiguationData":[OSD([sQuery(id+"F14.wireOp",EDGE,"E157.MirrorC")])],"isStart":false});
            var Q15;
            Q15=makeQuery(id+"F2.opExtrude","CAP_EDGE",EDGE,{"disambiguationData":[OSD([sQuery(id+"F0.wireOp",EDGE,"E8.MirrorC")])],"isStart":true});
            fillet(context, id + "F16", {"entities" : qUnion([Q0, Q1, Q2, Q3, Q4, Q5, Q6, Q7, Q8, Q9, Q10, Q11, Q12, Q13, Q14, Q15]), "radius" : .5 * mm, "tangentPropagation" : true, "allowEdgeOverflow" : false});
        }
    });
